# Revit family: DAL_A3-Double-Ext-Trad-(2)
name_source: partatom
category: Doors
revit_build: Autodesk Revit 2016 (Build: 20150220_1215(x64)
units: mm (PartAtom-declared; Revit-internal decimal feet)

## family parameters
Always vertical = Yes
Cut with Voids When Loaded = No
Host = Wall
Room Calculation Point = No
Shared = No

## types (2) — shared parameters
Cavity Closer Depth = 75 mm
Cavity Closer Offset from Ext = 102.5 mm  [stored 0.336286 ft]
Cavity Closer Width = 50 mm  [stored 0.164042 ft]
Cill Extension = 25 mm  [stored 0.082021 ft]
Cill Projection = 30 mm  [stored 0.0984252 ft]
Cill Thickness = 54.5 mm  [stored 0.178806 ft]
Door Panel Height (info only) = 2000 mm  [stored 6.56168 ft]
Ext Leaf Thickness (Scot) = 102.5 mm  [stored 0.336286 ft]
FrameDepth = 89 mm  [stored 0.291995 ft]
FrameOffset - External = 25 mm  [stored 0.082021 ft]
FrameWidth = 42 mm  [stored 0.137795 ft]
Function = Interior
Glazing Thickness = 24 mm  [stored 0.0787402 ft]
Handle X Distance = 75 mm
Handle Z Distance = 1050 mm  [stored 3.44488 ft]
Height = 2110 mm  [stored 6.92257 ft]
LeafThickness = 44 mm  [stored 0.144357 ft]
Material Glass = Glass
Material Iornmongery = Door - Handle
O/A Frame Width = 64 mm  [stored 0.209974 ft]
Operation = DoubleDoorSingleSwing
Rough Height = 2110 mm  [stored 6.92257 ft]
Stile - Bottom Rail = 175 mm  [stored 0.574147 ft]
Stile - Hanging = 100 mm  [stored 0.328084 ft]
Stile - Top Rail = 150 mm
Stile Shutting = 125 mm  [stored 0.410105 ft]
Structural Tolerance = 6.5 mm
Thickness = 44 mm  [stored 0.144357 ft]
Tolerance = 3 mm  [stored 0.00984252 ft]
Undercut = 4 mm  [stored 0.0131234 ft]
Vis - Cavity Closers = Yes
Vis - Ironmongery = Yes
Wall Closure = By host
Wrapping Layers from Int = 50 mm  [stored 0.164042 ft]
zero-valued in all types: Door Level, Ext Leaf Overlap (Scot)

## per-type parameters (varying)
| type | Door Panel Width (info only) | Rough Width | Width |
| 1810 x 2110mm | 852 mm | 1810 mm  [stored 5.93832 ft] | 1810 mm  [stored 5.93832 ft] |
| 1510 x 2110mm | 702 mm | 1510 mm  [stored 4.95407 ft] | 1510 mm  [stored 4.95407 ft] |

note: [stored X ft] marks values corroborated as IEEE doubles in the binary element streams (Revit-internal decimal feet)

## geometry (parser evidence)
native form markers: Sweep x4
no freeform markers — native parametric forms only
